FCSTD DOCUMENT  (FreeCAD 0.17R12920 (Git))
Label: sketch_lines
License: All rights reserved
LicenseURL: http://en.wikipedia.org/wiki/All_rights_reserved
objects: Sketcher::SketchObject×1
note: 1 computed .brp shape members not serialized (recipe doc carries the construction recipe); baked Part::Feature solids carry a one-line shape summary decoded from their .brp

FEATURE [Sketcher::SketchObject] Sketch
  sketch-geometry (6):
    g0: LineSegment StartX=4 StartY=8 StartZ=0 EndX=9 EndY=8 EndZ=0
    g1: LineSegment StartX=9 StartY=8 StartZ=0 EndX=9 EndY=2 EndZ=0
    g2: LineSegment StartX=9 StartY=2 StartZ=0 EndX=3 EndY=2 EndZ=0
    g3: LineSegment StartX=3 StartY=2 StartZ=0 EndX=3 EndY=7 EndZ=0
    g4: Circle CenterX=6 CenterY=5 CenterZ=0 NormalX=0 NormalY=0 NormalZ=1 AngleXU=0 Radius=2
    g5: ArcOfCircle CenterX=4 CenterY=7 CenterZ=0 NormalX=0 NormalY=0 NormalZ=1 AngleXU=0 Radius=1 StartAngle=1.5708 EndAngle=3.14159
  constraints (4):
    c: Coincident(g0,g1)
    c: Coincident(g1,g2)
    c: Coincident(g2,g3)
    c: Coincident(g3,g5)
